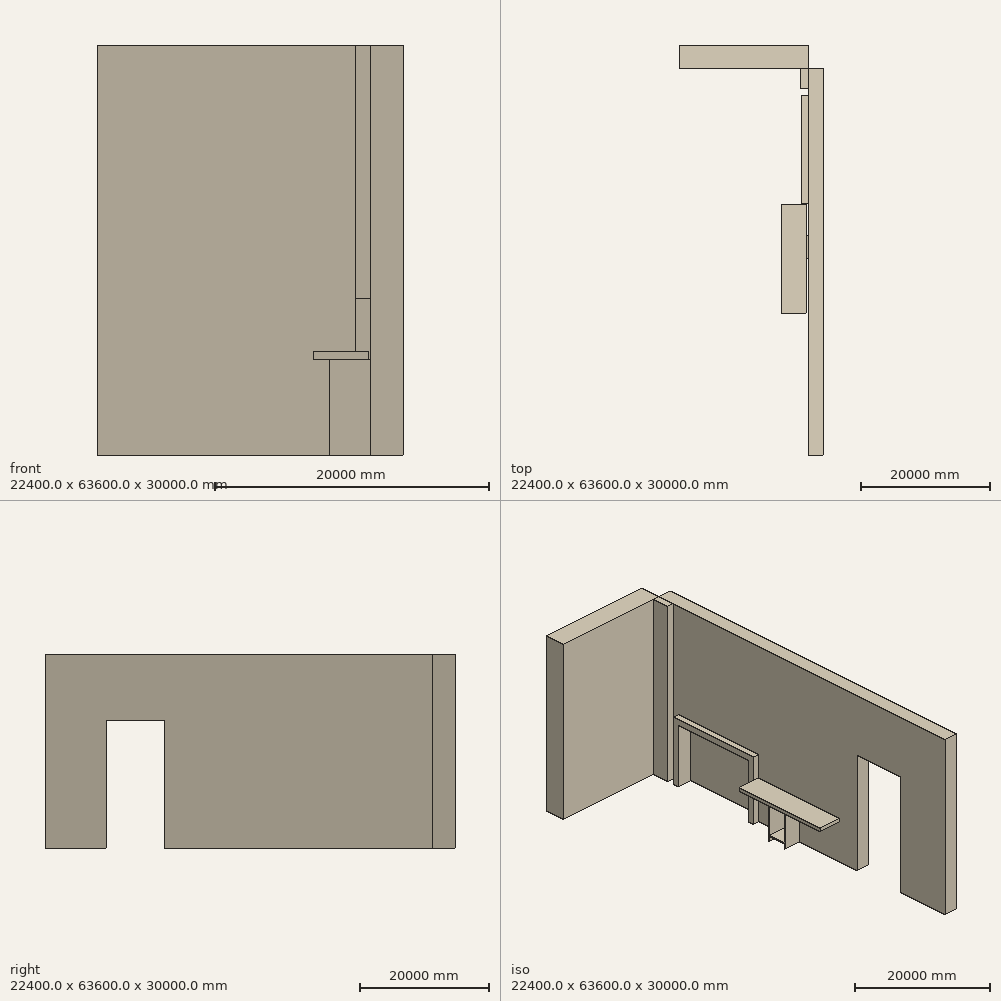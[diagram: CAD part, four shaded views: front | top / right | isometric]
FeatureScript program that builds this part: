
annotation { "Feature Type Name" : "Feature", "Feature Type Description" : "" }
export const myFeature = defineFeature(function(context is Context, id is Id, definition is map)
    precondition{}
    {
        {
            var Q0;
            Q0=qCreatedBy(makeId("Front.planeOp"),FACE);
            var sketch = newSketch(context, id + "F0", { "sketchPlane" : qUnion([Q0])});
            skLineSegment(sketch, "E0.bottom", {"start": v(-10025.39, 23230.62) * mm, "end": v(9974.61, 23230.62) * mm});
            skLineSegment(sketch, "E0.top", {"start": v(-10025.39, -6769.38) * mm, "end": v(9974.61, -6769.38) * mm});
            skLineSegment(sketch, "E0.left", {"start": v(-10025.39, 23230.62) * mm, "end": v(-10025.39, -6769.38) * mm});
            skLineSegment(sketch, "E0.right", {"start": v(9974.61, 23230.62) * mm, "end": v(9974.61, -6769.38) * mm});
            skSolve(sketch);
        }
        {
            var Q0;
            Q0=makeQuery(id+"F0.imprint","IMPRINT",FACE,{"disambiguationData":[TD([[makeQuery(id+"F0.imprint","IMPRINT",EDGE,{"derivedFrom":sQuery(id+"F0.wireOp",EDGE,"E0.bottom")}),-1.0]])]});
            extrude(context, id + "F1", {"entities" : qUnion([Q0]), "oppositeDirection" : true, "depth" : 3600 * mm});
        }
        {
            var Q0;
            Q0=makeQuery(id+"F1.opExtrude","SWEPT_FACE",FACE,{"disambiguationData":[OSD([sQuery(id+"F0.wireOp",EDGE,"E0.right")])]});
            var sketch = newSketch(context, id + "F2", { "sketchPlane" : qUnion([Q0])});
            skLineSegment(sketch, "E1.bottom", {"start": v(0, -6769.38) * mm, "end": v(-60000, -6769.38) * mm});
            skLineSegment(sketch, "E1.top", {"start": v(0, 23230.62) * mm, "end": v(-60000, 23230.62) * mm});
            skLineSegment(sketch, "E1.left", {"start": v(0, -6769.38) * mm, "end": v(0, 23230.62) * mm});
            skLineSegment(sketch, "E1.right", {"start": v(-60000, -6769.38) * mm, "end": v(-60000, 23230.62) * mm});
            skSolve(sketch);
        }
        {
            var Q0;
            Q0 = qSketchRegion(id + "F2", true);
            extrude(context, id + "F3", {"entities" : qUnion([Q0]), "depth" : 25 * mm});
        }
        {
            var Q0;
            Q0=makeQuery(id+"F3.opExtrude","CAP_FACE",FACE,{"disambiguationData":[OSD([sQuery(id+"F2.wireOp",EDGE,"E1.bottom"),sQuery(id+"F2.wireOp",EDGE,"E1.top"),sQuery(id+"F2.wireOp",EDGE,"E1.left"),sQuery(id+"F2.wireOp",EDGE,"E1.right")])],"isStart":true});
            extrude(context, id + "F4", {"entities" : qUnion([Q0]), "operationType" : NewBodyOperationType.ADD, "oppositeDirection" : true, "depth" : 2400 * mm});
        }
        {
            var Q0;
            Q0=makeQuery(id+"F1.opExtrude","SWEPT_FACE",FACE,{"disambiguationData":[OSD([sQuery(id+"F0.wireOp",EDGE,"E0.top")])]});
            var sketch = newSketch(context, id + "F5", { "sketchPlane" : qUnion([Q0])});
            skLineSegment(sketch, "E2.bottom", {"start": v(9974.61, 0) * mm, "end": v(8824.61, 0) * mm});
            skLineSegment(sketch, "E2.top", {"start": v(9974.61, 3000) * mm, "end": v(8824.61, 3000) * mm});
            skLineSegment(sketch, "E2.left", {"start": v(9974.61, 0) * mm, "end": v(9974.61, 3000) * mm});
            skLineSegment(sketch, "E2.right", {"start": v(8824.61, 0) * mm, "end": v(8824.61, 3000) * mm});
            skSolve(sketch);
        }
        {
            var Q0;
            Q0=makeQuery(id+"F5.imprint","IMPRINT",FACE,{"disambiguationData":[TD([[makeQuery(id+"F5.imprint","IMPRINT",EDGE,{"derivedFrom":sQuery(id+"F5.wireOp",EDGE,"E2.bottom")}),1.0]])]});
            extrude(context, id + "F6", {"entities" : qUnion([Q0]), "oppositeDirection" : true, "depth" : 30000 * mm});
        }
        {
            var Q0;
            Q0=makeQuery(id+"F3.opExtrude","CAP_FACE",FACE,{"disambiguationData":[OSD([sQuery(id+"F2.wireOp",EDGE,"E1.bottom"),sQuery(id+"F2.wireOp",EDGE,"E1.top"),sQuery(id+"F2.wireOp",EDGE,"E1.left"),sQuery(id+"F2.wireOp",EDGE,"E1.right")])],"isStart":true});
            var sketch = newSketch(context, id + "F7", { "sketchPlane" : qUnion([Q0])});
            skLineSegment(sketch, "E3.bottom", {"start": v(5200, -6769.38) * mm, "end": v(19950, -6769.38) * mm});
            skLineSegment(sketch, "E3.top", {"start": v(5200, 3730.62) * mm, "end": v(19950, 3730.62) * mm});
            skLineSegment(sketch, "E3.left", {"start": v(5200, -6769.38) * mm, "end": v(5200, 3730.62) * mm});
            skLineSegment(sketch, "E3.right", {"start": v(19950, -6769.38) * mm, "end": v(19950, 3730.62) * mm});
            skSolve(sketch);
        }
        {
            var Q0;
            Q0=makeQuery(id+"F7.imprint","IMPRINT",FACE,{"disambiguationData":[TD([[makeQuery(id+"F7.imprint","IMPRINT",EDGE,{"derivedFrom":sQuery(id+"F7.wireOp",EDGE,"E3.bottom")}),1.0]])]});
            extrude(context, id + "F8", {"entities" : qUnion([Q0]), "operationType" : NewBodyOperationType.REMOVE, "oppositeDirection" : true, "depth" : 1450 * mm});
        }
        {
            var Q0;
            Q0=makeQuery(id+"F3.opExtrude","CAP_FACE",FACE,{"disambiguationData":[OSD([sQuery(id+"F2.wireOp",EDGE,"E1.bottom"),sQuery(id+"F2.wireOp",EDGE,"E1.top"),sQuery(id+"F2.wireOp",EDGE,"E1.left"),sQuery(id+"F2.wireOp",EDGE,"E1.right")])],"isStart":true});
            var sketch = newSketch(context, id + "F9", { "sketchPlane" : qUnion([Q0])});
            skLineSegment(sketch, "E4.bottom", {"start": v(41550, -6769.38) * mm, "end": v(50550, -6769.38) * mm});
            skLineSegment(sketch, "E4.top", {"start": v(41550, 13030.62) * mm, "end": v(50550, 13030.62) * mm});
            skLineSegment(sketch, "E4.left", {"start": v(41550, -6769.38) * mm, "end": v(41550, 13030.62) * mm});
            skLineSegment(sketch, "E4.right", {"start": v(50550, -6769.38) * mm, "end": v(50550, 13030.62) * mm});
            skSolve(sketch);
        }
        {
            var Q0;
            Q0=makeQuery(id+"F9.imprint","IMPRINT",FACE,{"disambiguationData":[TD([[makeQuery(id+"F9.imprint","IMPRINT",EDGE,{"derivedFrom":sQuery(id+"F9.wireOp",EDGE,"E4.bottom")}),1.0]])]});
            extrude(context, id + "F10", {"entities" : qUnion([Q0]), "operationType" : NewBodyOperationType.REMOVE, "oppositeDirection" : true, "depth" : 3000 * mm});
        }
        {
            var Q0;
            Q0=makeQuery(id+"F3.opExtrude","CAP_FACE",FACE,{"disambiguationData":[OSD([sQuery(id+"F2.wireOp",EDGE,"E1.bottom"),sQuery(id+"F2.wireOp",EDGE,"E1.top"),sQuery(id+"F2.wireOp",EDGE,"E1.left"),sQuery(id+"F2.wireOp",EDGE,"E1.right")])],"isStart":true});
            var sketch = newSketch(context, id + "F11", { "sketchPlane" : qUnion([Q0])});
            skLineSegment(sketch, "E5.bottom", {"start": v(25950, 230.62) * mm, "end": v(29450, 230.62) * mm});
            skLineSegment(sketch, "E5.left", {"start": v(25950, 230.62) * mm, "end": v(25950, -6764.38) * mm});
            skLineSegment(sketch, "E5.right", {"start": v(29450, 230.62) * mm, "end": v(29450, -6764.38) * mm});
            skLineSegment(sketch, "E6", {"start": v(25955, -6769.38) * mm, "end": v(26150, -6769.38) * mm});
            skArc(sketch, "E7.filletArc", {"start": v(25950, -6764.38) * mm, "mid": v(25951.46, -6767.92) * mm, "end": v(25955, -6769.38) * mm});
            skArc(sketch, "E8.filletArc", {"start": v(29445, -6769.38) * mm, "mid": v(29448.54, -6767.92) * mm, "end": v(29450, -6764.38) * mm});
            skLineSegment(sketch, "E9", {"start": v(26150, -5969.38) * mm, "end": v(29250, -5969.38) * mm});
            skLineSegment(sketch, "E10", {"start": v(29250, -5969.38) * mm, "end": v(29250, -6769.38) * mm});
            skLineSegment(sketch, "E11", {"start": v(26150, -5969.38) * mm, "end": v(26150, -6769.38) * mm});
            skLineSegment(sketch, "E12.trimOffspring", {"start": v(29250, -6769.38) * mm, "end": v(29445, -6769.38) * mm});
            skSolve(sketch);
        }
        {
            var Q0;
            Q0=makeQuery(id+"F11.imprint","IMPRINT",FACE,{"disambiguationData":[TD([[makeQuery(id+"F11.imprint","IMPRINT",EDGE,{"derivedFrom":sQuery(id+"F11.wireOp",EDGE,"E5.bottom")}),1.0]])]});
            var sketch = newSketch(context, id + "F12", { "sketchPlane" : qUnion([Q0])});
            skLineSegment(sketch, "E13.left", {"start": v(5200, -6769.38) * mm, "end": v(5200, 3730.62) * mm});
            skLineSegment(sketch, "E13.right", {"start": v(19950, -6769.38) * mm, "end": v(19950, 3730.62) * mm});
            skLineSegment(sketch, "E14", {"start": v(20950, 4730.62) * mm, "end": v(20950, -6769.38) * mm});
            skLineSegment(sketch, "E15", {"start": v(20950, -6769.38) * mm, "end": v(19950, -6769.38) * mm});
            skLineSegment(sketch, "E16", {"start": v(5200, -6769.38) * mm, "end": v(4200, -6769.38) * mm});
            skLineSegment(sketch, "E17", {"start": v(4200, -6769.38) * mm, "end": v(4200, 4730.62) * mm});
            skLineSegment(sketch, "E18", {"start": v(5200, 3730.62) * mm, "end": v(19950, 3730.62) * mm});
            skLineSegment(sketch, "E19", {"start": v(4200, 4730.62) * mm, "end": v(20950, 4730.62) * mm});
            skSolve(sketch);
        }
        {
            var Q0;
            Q0=makeQuery(id+"F12.imprint","IMPRINT",FACE,{"disambiguationData":[TD([[makeQuery(id+"F12.imprint","IMPRINT",EDGE,{"derivedFrom":sQuery(id+"F12.wireOp",EDGE,"E13.left")}),1.0]])]});
            extrude(context, id + "F13", {"entities" : qUnion([Q0]), "operationType" : NewBodyOperationType.ADD, "offsetDistance" : 25 * mm, "depth" : 1100 * mm});
        }
        {
            var Q0;
            Q0 = qSketchRegion(id + "F11", true);
            extrude(context, id + "F14", {"entities" : qUnion([Q0]), "operationType" : NewBodyOperationType.ADD, "depth" : 3000 * mm, "offsetDistance" : 25 * mm});
        }
        {
            var Q0;
            Q0=makeQuery(id+"F14.opExtrude","CAP_FACE",FACE,{"disambiguationData":[OSD([sQuery(id+"F11.wireOp",EDGE,"E5.bottom"),sQuery(id+"F11.wireOp",EDGE,"E5.left"),sQuery(id+"F11.wireOp",EDGE,"E5.right"),sQuery(id+"F11.wireOp",EDGE,"E6"),sQuery(id+"F11.wireOp",EDGE,"E7.filletArc"),sQuery(id+"F11.wireOp",EDGE,"E8.filletArc")])],"isStart":false});
            shell(context, id + "F15", {"entities" : qUnion([Q0]), "thickness" : 200 * mm});
        }
        {
            var Q0;
            Q0=makeQuery(id+"F6.opExtrude","SWEPT_FACE",FACE,{"disambiguationData":[OSD([sQuery(id+"F5.wireOp",EDGE,"E2.top")])]});
            var sketch = newSketch(context, id + "F16", { "sketchPlane" : qUnion([Q0])});
            skLineSegment(sketch, "E20.bottom", {"start": v(5774.61, 230.62) * mm, "end": v(9774.61, 230.62) * mm});
            skLineSegment(sketch, "E20.left", {"start": v(5774.61, 230.62) * mm, "end": v(5774.61, 830.62) * mm});
            skLineSegment(sketch, "E21", {"start": v(9774.61, 230.62) * mm, "end": v(9774.61, 830.62) * mm});
            skLineSegment(sketch, "E22", {"start": v(5774.61, 830.62) * mm, "end": v(9774.61, 830.62) * mm});
            skSolve(sketch);
        }
        {
            var Q0;
            Q0 = qSketchRegion(id + "F16", true);
            extrude(context, id + "F17", {"entities" : qUnion([Q0]), "operationType" : NewBodyOperationType.ADD, "depth" : 35000 * mm, "offsetDistance" : 25 * mm, "hasSecondDirection" : true, "secondDirectionOppositeDirection" : false, "secondDirectionDepth" : 18000 * mm});
        }
    });
